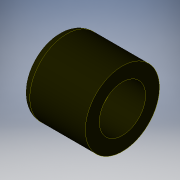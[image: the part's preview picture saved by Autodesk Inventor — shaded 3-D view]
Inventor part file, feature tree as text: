
AUTODESK INVENTOR PART (.ipt)
format: ipt  version: 2019 (Build 230136000, 136)  size: 137,216 bytes
history: native  units: mm
features: other x7, revolve x1, sketch x1
ambient origin geometry x8: Origin, YZ Plane, XZ Plane, XY Plane, X Axis, Y Axis, Z Axis, Center Point
bodies: Solid1 (feature_tree)
feature tree (9):
  revolve  "Revolution1"  [1 undecoded]
  other  "pusher_XY"
  other  "pusher_YZ"
  other  "pusher_ZX"
  other  "pusher_X"
  other  "pusher_Y"
  other  "pusher_Z"
  other  "pusher_Center"
  sketch  "Sketch_1"  dims[d0=360.0deg d1=0.0mm]
note: 1 required parameter value undecoded (feature->parameter linkage not recoverable at this tier; creation-order binding heuristic only, values carry confidence <= 0.55)
